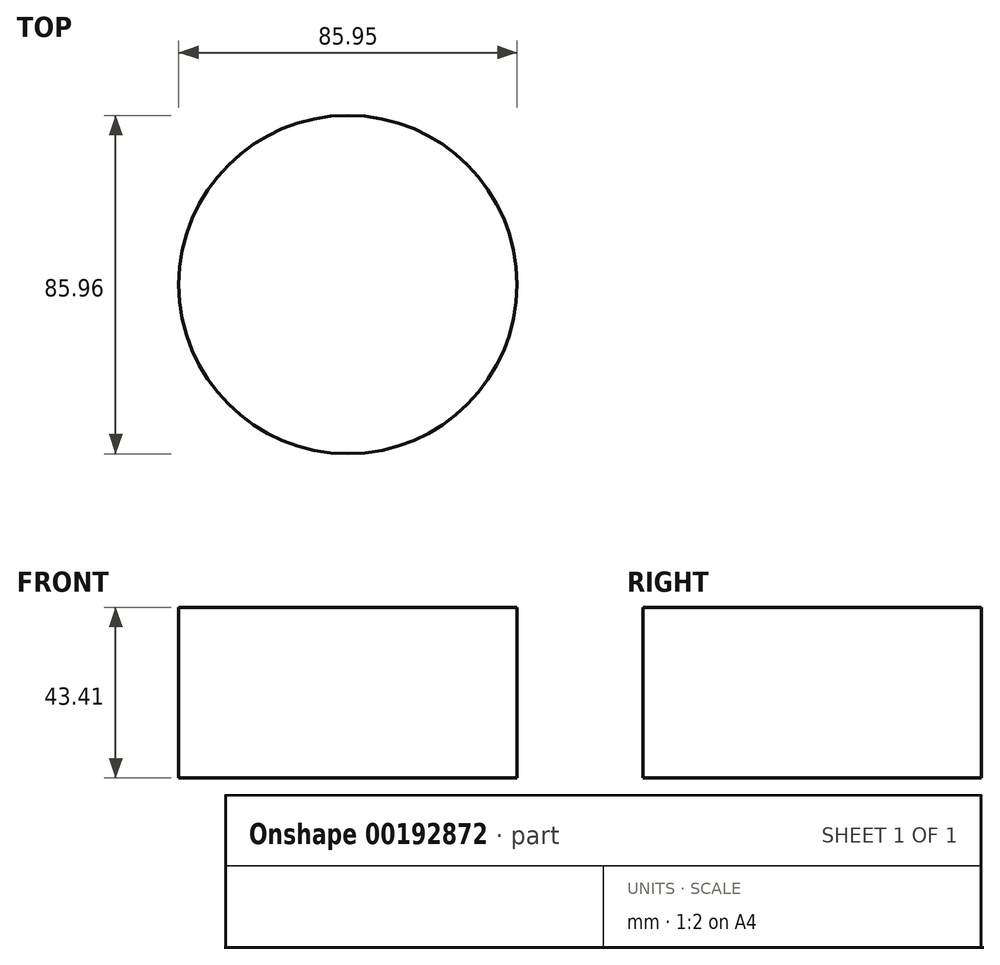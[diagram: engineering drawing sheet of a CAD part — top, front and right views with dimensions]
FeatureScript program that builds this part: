
annotation { "Feature Type Name" : "Feature", "Feature Type Description" : "" }
export const myFeature = defineFeature(function(context is Context, id is Id, definition is map)
    precondition{}
    {
        {
            var Q0;
            Q0=qCreatedBy(makeId("Front.planeOp"),FACE);
            var sketch = newSketch(context, id + "F0", { "sketchPlane" : qUnion([Q0])});
            skLineSegment(sketch, "E0.bottom", {"start": v(0.43, -1.52) * mm, "end": v(43.41, -1.52) * mm});
            skLineSegment(sketch, "E0.top", {"start": v(0.43, -44.93) * mm, "end": v(43.41, -44.93) * mm});
            skLineSegment(sketch, "E0.left", {"start": v(0.43, -1.52) * mm, "end": v(0.43, -44.93) * mm});
            skLineSegment(sketch, "E0.right", {"start": v(43.41, -1.52) * mm, "end": v(43.41, -44.93) * mm});
            skSolve(sketch);
        }
        {
            var Q0;
            Q0=makeQuery(id+"F0.imprint","IMPRINT",FACE,{"disambiguationData":[TD([[makeQuery(id+"F0.imprint","IMPRINT",EDGE,{"derivedFrom":sQuery(id+"F0.wireOp",EDGE,"E0.bottom")}),-1.0]])]});
            var Q1;
            Q1=sQuery(id+"F0.wireOp",EDGE,"E0.left");
            revolve(context, id + "F1", {"entities" : qUnion([Q0]), "axis" : qUnion([Q1]), "revolveType" : RevolveType.FULL});
        }
        {
            var Q0;
            Q0=qCreatedBy(makeId("Right.planeOp"),FACE);
            var sketch = newSketch(context, id + "F2", { "sketchPlane" : qUnion([Q0])});
            skLineSegment(sketch, "E1", {"start": v(0, 67.68) * mm, "end": v(35.31, 57.31) * mm});
            skLineSegment(sketch, "E2", {"start": v(35.31, 57.31) * mm, "end": v(21.58, 38.53) * mm});
            skLineSegment(sketch, "E3", {"start": v(21.58, 38.53) * mm, "end": v(43.16, -2.66) * mm});
            skSolve(sketch);
        }
    });
